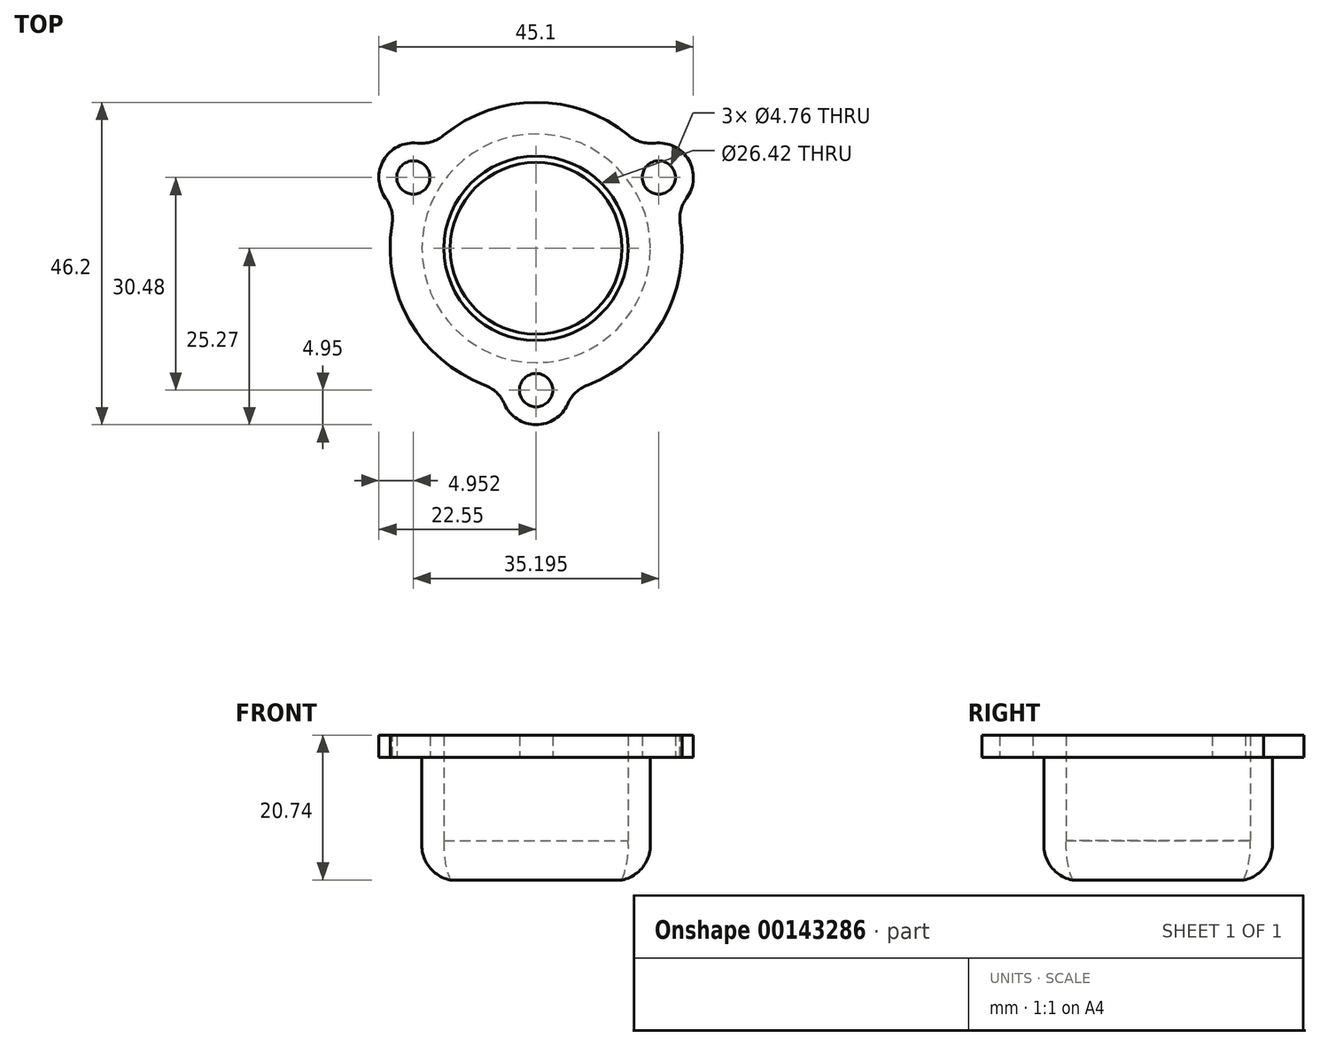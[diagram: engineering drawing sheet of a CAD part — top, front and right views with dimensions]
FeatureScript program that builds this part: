
annotation { "Feature Type Name" : "Feature", "Feature Type Description" : "" }
export const myFeature = defineFeature(function(context is Context, id is Id, definition is map)
    precondition{}
    {
        {
            var Q0;
            Q0=qCreatedBy(makeId("Front.planeOp"),FACE);
            var sketch = newSketch(context, id + "F0", { "sketchPlane" : qUnion([Q0])});
            skCircle(sketch, "E0", {"center": v(0, -12.7) * mm, "radius": 12.7 * mm});
            skLineSegment(sketch, "E1", {"start": v(-12.7, 3.17) * mm, "end": v(12.7, 3.17) * mm});
            skLineSegment(sketch, "E2", {"start": v(12.7, 3.17) * mm, "end": v(-6.95, 3.17) * mm});
            skLineSegment(sketch, "E3", {"start": v(-12.7, 3.17) * mm, "end": v(-12.7, -22.23) * mm});
            skLineSegment(sketch, "E4", {"start": v(-12.7, -22.23) * mm, "end": v(-12.7, 3.17) * mm});
            skLineSegment(sketch, "E5", {"start": v(12.7, 3.17) * mm, "end": v(12.7, -22.22) * mm});
            skLineSegment(sketch, "E6", {"start": v(12.7, -22.22) * mm, "end": v(12.7, 3.17) * mm});
            skCircle(sketch, "E7", {"center": v(-9.53, 0) * mm, "radius": 3.18 * mm});
            skPoint(sketch, "E8.visualSharp", {"position": v(-12.7, 3.17) * mm});
            skCircle(sketch, "E9", {"center": v(9.52, 0) * mm, "radius": 3.18 * mm});
            skLineSegment(sketch, "E10", {"start": v(-9.53, 0) * mm, "end": v(9.52, 0) * mm});
            skPoint(sketch, "E11", {"position": v(0, 0) * mm});
            skLineSegment(sketch, "E12", {"start": v(-12.7, -22.23) * mm, "end": v(-9.52, -22.23) * mm});
            skLineSegment(sketch, "E13", {"start": v(-9.52, -22.23) * mm, "end": v(-12.7, -22.23) * mm});
            skLineSegment(sketch, "E14", {"start": v(12.7, -22.22) * mm, "end": v(9.52, -22.22) * mm});
            skLineSegment(sketch, "E15", {"start": v(9.52, -22.22) * mm, "end": v(12.7, -22.22) * mm});
            skArc(sketch, "E16", {"start": v(-12.7, -17.2) * mm, "mid": v(-11.4, -19.89) * mm, "end": v(-9.52, -22.23) * mm});
            skArc(sketch, "E17", {"start": v(9.52, -22.22) * mm, "mid": v(11.4, -19.89) * mm, "end": v(12.7, -17.2) * mm});
            skSolve(sketch);
        }
        {
            var Q0;
            Q0=qCreatedBy(makeId("Front.planeOp"),FACE);
            var sketch = newSketch(context, id + "F1", { "sketchPlane" : qUnion([Q0])});
            skLineSegment(sketch, "E18", {"start": v(12.3, -17.56) * mm, "end": v(16.38, -17.56) * mm});
            skLineSegment(sketch, "E19", {"start": v(16.38, -17.56) * mm, "end": v(16.38, 3.17) * mm});
            skLineSegment(sketch, "E20", {"start": v(0, 3.17) * mm, "end": v(13.2, 3.18) * mm});
            skLineSegment(sketch, "E21", {"start": v(13.2, 3.17) * mm, "end": v(13.2, -11.92) * mm});
            skLineSegment(sketch, "E22", {"start": v(13.2, -11.92) * mm, "end": v(13.2, 3.17) * mm});
            skLineSegment(sketch, "E23", {"start": v(16.38, 3.17) * mm, "end": v(13.2, 3.17) * mm});
            skLineSegment(sketch, "E24", {"start": v(13.2, 3.17) * mm, "end": v(13.2, 3.17) * mm});
            skLineSegment(sketch, "E25", {"start": v(16.38, 3.17) * mm, "end": v(25.27, 3.17) * mm});
            skLineSegment(sketch, "E26", {"start": v(25.27, 3.17) * mm, "end": v(25.27, 0) * mm});
            skLineSegment(sketch, "E27", {"start": v(25.27, 0) * mm, "end": v(16.38, 0) * mm});
            skArc(sketch, "E28", {"start": v(12.3, -17.56) * mm, "mid": v(13.07, -14.79) * mm, "end": v(13.2, -11.92) * mm});
            skLineSegment(sketch, "E29", {"start": v(0, 3.17) * mm, "end": v(0, -22.11) * mm});
            skLineSegment(sketch, "E30", {"start": v(0, -22.11) * mm, "end": v(0, 3.17) * mm});
            skSolve(sketch);
        }
        {
            var Q0;
            {var subQ3=sQuery(id+"F1.wireOp",EDGE,"E18");Q0=makeQuery(id+"F1.imprint","IMPRINT",FACE,{"disambiguationData":[TD([[makeQuery(id+"F1.imprint","IMPRINT",EDGE,{"derivedFrom":subQ3}),1.0]])]});}
            var Q1;
            {var subQ0=sQuery(id+"F1.wireOp",EDGE,"E25");Q1=makeQuery(id+"F1.imprint","IMPRINT",FACE,{"disambiguationData":[TD([[makeQuery(id+"F1.imprint","IMPRINT",EDGE,{"derivedFrom":subQ0}),-1.0]])]});}
            var Q2;
            Q2=sQuery(id+"F1.wireOp",EDGE,"E30");
            revolve(context, id + "F2", {"surfaceOperationType" : NewSurfaceOperationType.NEW, "entities" : qUnion([Q0, Q1]), "axis" : qUnion([Q2]), "revolveType" : RevolveType.FULL});
        }
        {
            var Q0;
            Q0=makeQuery(id+"F2.opRevolve","SWEPT_FACE",FACE,{"disambiguationData":[OSD([sQuery(id+"F1.wireOp",EDGE,"E27")])]});
            var sketch = newSketch(context, id + "F3", { "sketchPlane" : qUnion([Q0])});
            skLineSegment(sketch, "E31", {"start": v(0, 0) * mm, "end": v(0, 20.32) * mm});
            skCircle(sketch, "E32", {"center": v(0, 20.32) * mm, "radius": 2.38 * mm});
            skCircle(sketch, "E33.1.0", {"center": v(-17.6, -10.16) * mm, "radius": 2.38 * mm});
            skCircle(sketch, "E33.2.0", {"center": v(17.6, -10.16) * mm, "radius": 2.38 * mm});
            skPoint(sketch, "E33.center", {"position": v(0, 0) * mm});
            skSolve(sketch);
        }
        {
            var Q0;
            Q0 = qSketchRegion(id + "F3", true);
            extrude(context, id + "F4", {"entities" : qUnion([Q0]), "operationType" : NewBodyOperationType.REMOVE, "endBound" : BoundingType.THROUGH_ALL, "oppositeDirection" : true, "depth" : 25.4 * mm, "offsetDistance" : 25.4 * mm});
        }
        {
            var Q0;
            Q0=makeQuery(id+"F2.opRevolve","SWEPT_EDGE",EDGE,{"disambiguationData":[OSD([sQuery(id+"F1.wireOp",EDGE,"E18"),sQuery(id+"F1.wireOp",EDGE,"E19")])]});
            fillet(context, id + "F5", {"entities" : qUnion([Q0]), "radius" : 5.08 * mm, "tangentPropagation" : true, "allowEdgeOverflow" : false});
        }
        {
            var Q0;
            Q0=makeQuery(id+"F2.opRevolve","SWEPT_FACE",FACE,{"disambiguationData":[OSD([sQuery(id+"F1.wireOp",EDGE,"E27")])]});
            var sketch = newSketch(context, id + "F6", { "sketchPlane" : qUnion([Q0])});
            skCircle(sketch, "E34", {"center": v(0, 20.32) * mm, "radius": 4.95 * mm});
            skCircle(sketch, "E35", {"center": v(17.6, -10.16) * mm, "radius": 4.95 * mm});
            skCircle(sketch, "E36", {"center": v(-17.6, -10.16) * mm, "radius": 4.95 * mm});
            skArc(sketch, "E37", {"start": v(-4.95, 20.34) * mm, "mid": v(-18.13, 10.47) * mm, "end": v(-20.1, -5.88) * mm});
            skArc(sketch, "E38.1.0", {"start": v(-15.14, -14.46) * mm, "mid": v(0, -20.93) * mm, "end": v(15.14, -14.46) * mm});
            skArc(sketch, "E38.2.0", {"start": v(20.1, -5.88) * mm, "mid": v(18.13, 10.47) * mm, "end": v(4.95, 20.34) * mm});
            skCircle(sketch, "E39", {"center": v(0, 0) * mm, "radius": 25.27 * mm});
            skSolve(sketch);
        }
        {
            var Q0;
            {var subQ0=sQuery(id+"F6.wireOp",EDGE,"E37");Q0=makeQuery(id+"F6.imprint","IMPRINT",FACE,{"disambiguationData":[TD([[makeQuery(id+"F6.imprint","IMPRINT",EDGE,{"derivedFrom":subQ0}),-1.0]])]});}
            var Q1;
            {var subQ0=sQuery(id+"F6.wireOp",EDGE,"E38.2.0");Q1=makeQuery(id+"F6.imprint","IMPRINT",FACE,{"disambiguationData":[TD([[makeQuery(id+"F6.imprint","IMPRINT",EDGE,{"derivedFrom":subQ0}),-1.0]])]});}
            var Q2;
            {var subQ0=sQuery(id+"F6.wireOp",EDGE,"E38.1.0");Q2=makeQuery(id+"F6.imprint","IMPRINT",FACE,{"disambiguationData":[TD([[makeQuery(id+"F6.imprint","IMPRINT",EDGE,{"derivedFrom":subQ0}),-1.0]])]});}
            extrude(context, id + "F7", {"entities" : qUnion([Q0, Q1, Q2]), "operationType" : NewBodyOperationType.REMOVE, "endBound" : BoundingType.THROUGH_ALL, "oppositeDirection" : true, "depth" : 25.4 * mm, "offsetDistance" : 25.4 * mm});
        }
        {
            var Q0;
            Q0=makeQuery(id+"F7.boolean.opBoolean","COPY",EDGE,{"derivedFrom":makeQuery(id+"F7.opExtrude","SWEPT_EDGE",EDGE,{"disambiguationData":[OSD([sQuery(id+"F6.wireOp",EDGE,"E36"),sQuery(id+"F6.wireOp",EDGE,"E38.1.0")])]})});
            var Q1;
            Q1=makeQuery(id+"F7.boolean.opBoolean","COPY",EDGE,{"derivedFrom":makeQuery(id+"F7.opExtrude","SWEPT_EDGE",EDGE,{"disambiguationData":[OSD([sQuery(id+"F6.wireOp",EDGE,"E35"),sQuery(id+"F6.wireOp",EDGE,"E38.1.0")])]})});
            var Q2;
            Q2=makeQuery(id+"F7.boolean.opBoolean","COPY",EDGE,{"derivedFrom":makeQuery(id+"F7.opExtrude","SWEPT_EDGE",EDGE,{"disambiguationData":[OSD([sQuery(id+"F6.wireOp",EDGE,"E35"),sQuery(id+"F6.wireOp",EDGE,"E38.2.0")])]})});
            var Q3;
            Q3=makeQuery(id+"F7.boolean.opBoolean","COPY",EDGE,{"derivedFrom":makeQuery(id+"F7.opExtrude","SWEPT_EDGE",EDGE,{"disambiguationData":[OSD([sQuery(id+"F6.wireOp",EDGE,"E34"),sQuery(id+"F6.wireOp",EDGE,"E38.2.0")])]})});
            var Q4;
            Q4=makeQuery(id+"F7.boolean.opBoolean","COPY",EDGE,{"derivedFrom":makeQuery(id+"F7.opExtrude","SWEPT_EDGE",EDGE,{"disambiguationData":[OSD([sQuery(id+"F6.wireOp",EDGE,"E34"),sQuery(id+"F6.wireOp",EDGE,"E37")])]})});
            var Q5;
            Q5=makeQuery(id+"F7.boolean.opBoolean","COPY",EDGE,{"derivedFrom":makeQuery(id+"F7.opExtrude","SWEPT_EDGE",EDGE,{"disambiguationData":[OSD([sQuery(id+"F6.wireOp",EDGE,"E36"),sQuery(id+"F6.wireOp",EDGE,"E37")])]})});
            fillet(context, id + "F8", {"entities" : qUnion([Q0, Q1, Q2, Q3, Q4, Q5]), "radius" : 5.08 * mm, "tangentPropagation" : true, "allowEdgeOverflow" : false});
        }
    });
